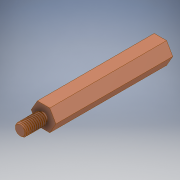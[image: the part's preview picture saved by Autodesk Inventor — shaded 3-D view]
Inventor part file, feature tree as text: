
AUTODESK INVENTOR PART (.ipt)
format: ipt  version: 2020 (Build 240168000, 168)  size: 2,296,832 bytes
history: native  units: mm
features: other x1, extrude x1, sketch x1, projected_geometry x1, imported_body x1
ambient origin geometry x8: Origin, YZ Plane, XZ Plane, XY Plane, X Axis, Y Axis, Z Axis, Center Point
bodies: Body1 (feature_tree)
feature tree (5):
  other  "Твердое тело1"
  extrude  "Выдавливание1"  Depth=5.0mm TaperAngle=0.0deg
  sketch  "Эскиз1"
  projected_geometry  "Спроецированная петля1"
  imported_body  "БазТело1"
